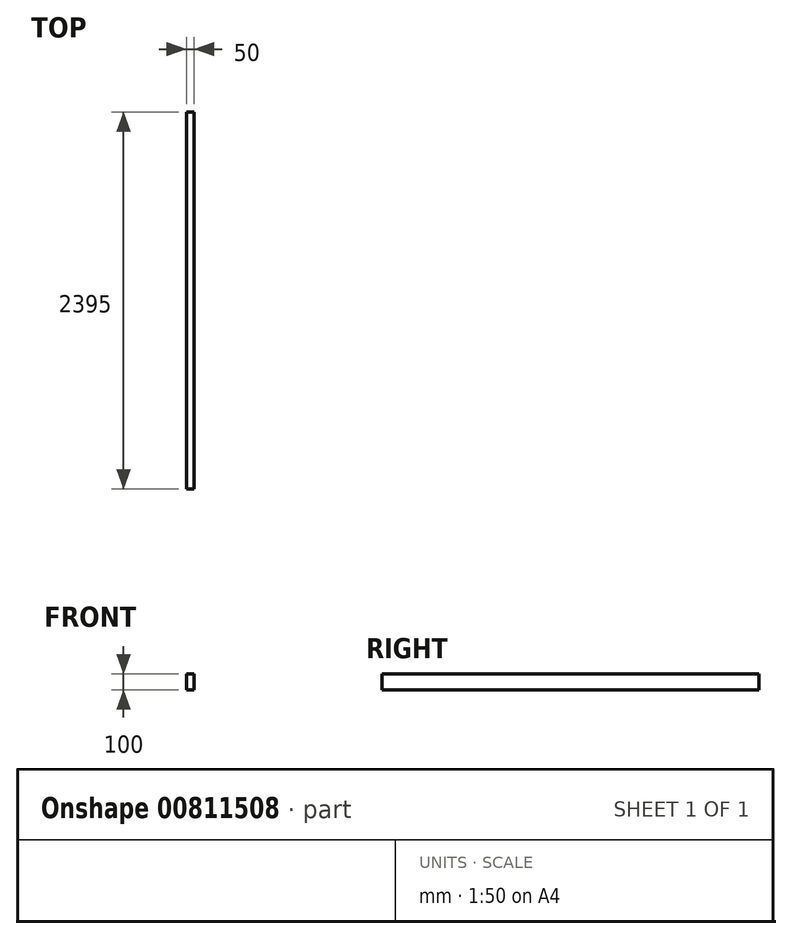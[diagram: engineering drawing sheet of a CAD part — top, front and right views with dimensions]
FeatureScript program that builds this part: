
annotation { "Feature Type Name" : "Feature", "Feature Type Description" : "" }
export const myFeature = defineFeature(function(context is Context, id is Id, definition is map)
    precondition{}
    {
        {
            var Q0;
            Q0=qCreatedBy(makeId("Front.planeOp"),FACE);
            var sketch = newSketch(context, id + "F0", { "sketchPlane" : qUnion([Q0])});
            skLineSegment(sketch, "E0.bottom", {"start": v(25, 50) * mm, "end": v(-25, 50) * mm});
            skLineSegment(sketch, "E0.top", {"start": v(25, -50) * mm, "end": v(-25, -50) * mm});
            skLineSegment(sketch, "E0.left", {"start": v(25, 50) * mm, "end": v(25, -50) * mm});
            skLineSegment(sketch, "E0.right", {"start": v(-25, 50) * mm, "end": v(-25, -50) * mm});
            skPoint(sketch, "E0.middle", {"position": v(0, 0) * mm});
            skSolve(sketch);
        }
        {
            var Q0;
            Q0=makeQuery(id+"F0.imprint","IMPRINT",FACE,{"disambiguationData":[TD([[makeQuery(id+"F0.imprint","IMPRINT",EDGE,{"derivedFrom":sQuery(id+"F0.wireOp",EDGE,"E0.bottom")}),1.0]])]});
            extrude(context, id + "F1", {"entities" : qUnion([Q0]), "endBound" : BoundingType.SYMMETRIC, "depth" : 2395 * mm, "offsetDistance" : 25.4 * mm});
        }
    });
